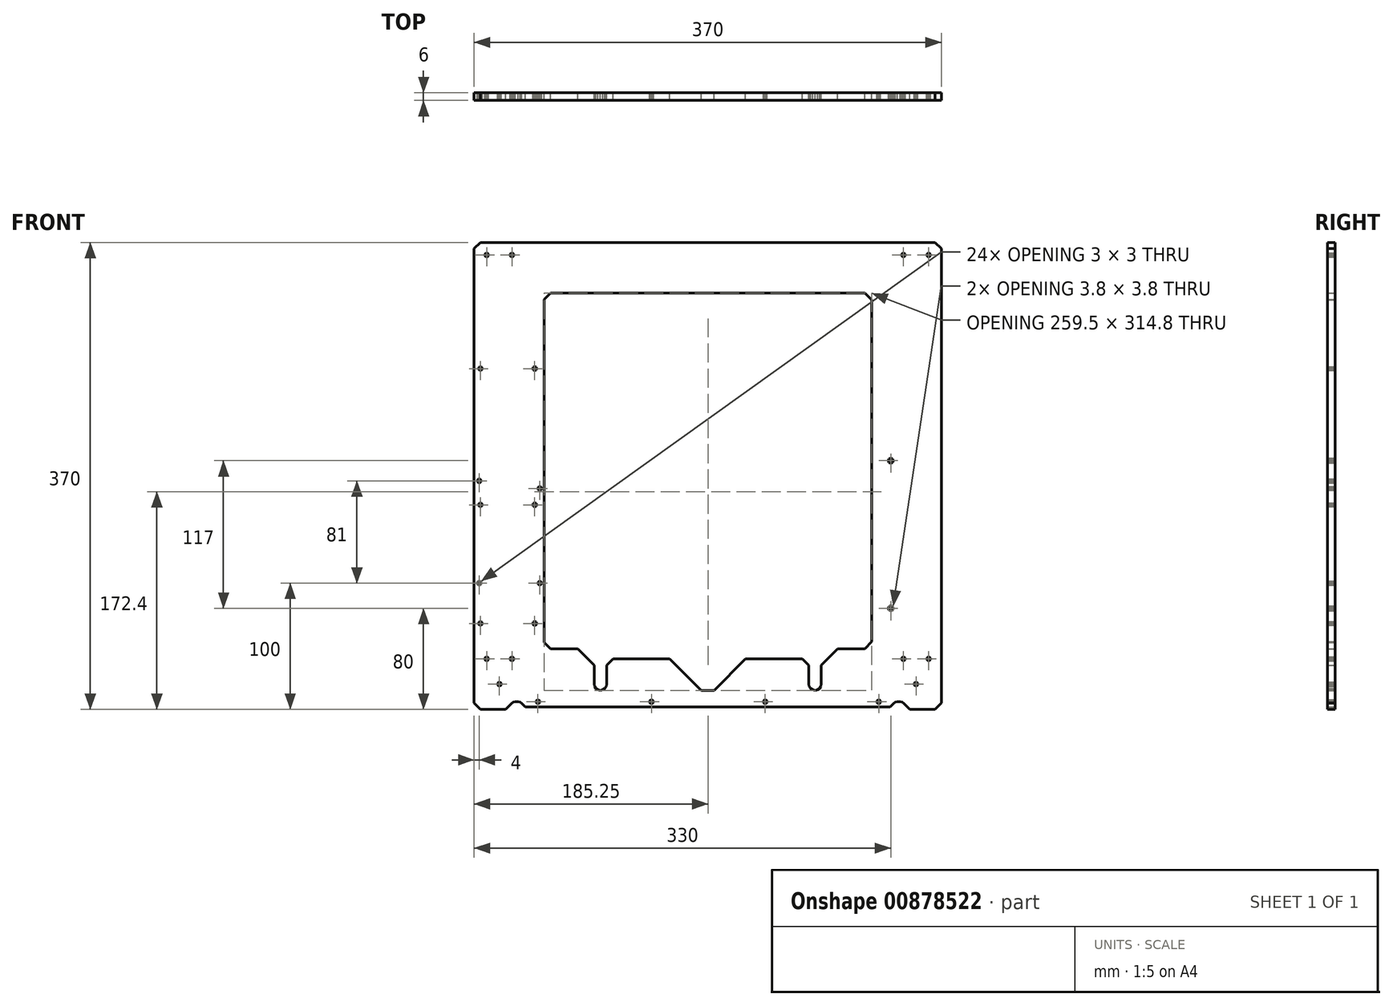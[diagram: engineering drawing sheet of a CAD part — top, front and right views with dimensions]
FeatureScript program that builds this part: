
annotation { "Feature Type Name" : "Feature", "Feature Type Description" : "" }
export const myFeature = defineFeature(function(context is Context, id is Id, definition is map)
    precondition{}
    {
        {
            var Q0;
            Q0=qCreatedBy(makeId("Front.planeOp"),FACE);
            var sketch = newSketch(context, id + "F0", { "sketchPlane" : qUnion([Q0])});
            skLineSegment(sketch, "E0", {"start": v(176.5, -145) * mm, "end": v(176.39, -145.57) * mm});
            skLineSegment(sketch, "E1", {"start": v(176.39, -145.57) * mm, "end": v(176.06, -146.06) * mm});
            skLineSegment(sketch, "E2", {"start": v(176.06, -146.06) * mm, "end": v(175.57, -146.39) * mm});
            skLineSegment(sketch, "E3", {"start": v(175.57, -146.39) * mm, "end": v(175, -146.5) * mm});
            skLineSegment(sketch, "E4", {"start": v(175, -146.5) * mm, "end": v(174.43, -146.39) * mm});
            skLineSegment(sketch, "E5", {"start": v(174.43, -146.39) * mm, "end": v(173.94, -146.06) * mm});
            skLineSegment(sketch, "E6", {"start": v(173.94, -146.06) * mm, "end": v(173.61, -145.57) * mm});
            skLineSegment(sketch, "E7", {"start": v(173.61, -145.57) * mm, "end": v(173.5, -145) * mm});
            skLineSegment(sketch, "E8", {"start": v(173.5, -145) * mm, "end": v(173.61, -144.43) * mm});
            skLineSegment(sketch, "E9", {"start": v(173.61, -144.43) * mm, "end": v(173.94, -143.94) * mm});
            skLineSegment(sketch, "E10", {"start": v(173.94, -143.94) * mm, "end": v(174.43, -143.61) * mm});
            skLineSegment(sketch, "E11", {"start": v(174.43, -143.61) * mm, "end": v(175, -143.5) * mm});
            skLineSegment(sketch, "E12", {"start": v(175, -143.5) * mm, "end": v(175.57, -143.61) * mm});
            skLineSegment(sketch, "E13", {"start": v(175.57, -143.61) * mm, "end": v(176.06, -143.94) * mm});
            skLineSegment(sketch, "E14", {"start": v(176.06, -143.94) * mm, "end": v(176.39, -144.43) * mm});
            skLineSegment(sketch, "E15", {"start": v(176.39, -144.43) * mm, "end": v(176.5, -145) * mm});
            skLineSegment(sketch, "E16", {"start": v(176.5, 175) * mm, "end": v(176.39, 174.43) * mm});
            skLineSegment(sketch, "E17", {"start": v(176.39, 174.43) * mm, "end": v(176.06, 173.94) * mm});
            skLineSegment(sketch, "E18", {"start": v(176.06, 173.94) * mm, "end": v(175.57, 173.61) * mm});
            skLineSegment(sketch, "E19", {"start": v(175.57, 173.61) * mm, "end": v(175, 173.5) * mm});
            skLineSegment(sketch, "E20", {"start": v(175, 173.5) * mm, "end": v(174.43, 173.61) * mm});
            skLineSegment(sketch, "E21", {"start": v(174.43, 173.61) * mm, "end": v(173.94, 173.94) * mm});
            skLineSegment(sketch, "E22", {"start": v(173.94, 173.94) * mm, "end": v(173.61, 174.43) * mm});
            skLineSegment(sketch, "E23", {"start": v(173.61, 174.43) * mm, "end": v(173.5, 175) * mm});
            skLineSegment(sketch, "E24", {"start": v(173.5, 175) * mm, "end": v(173.61, 175.57) * mm});
            skLineSegment(sketch, "E25", {"start": v(173.61, 175.57) * mm, "end": v(173.94, 176.06) * mm});
            skLineSegment(sketch, "E26", {"start": v(173.94, 176.06) * mm, "end": v(174.43, 176.39) * mm});
            skLineSegment(sketch, "E27", {"start": v(174.43, 176.39) * mm, "end": v(175, 176.5) * mm});
            skLineSegment(sketch, "E28", {"start": v(175, 176.5) * mm, "end": v(175.57, 176.39) * mm});
            skLineSegment(sketch, "E29", {"start": v(175.57, 176.39) * mm, "end": v(176.06, 176.06) * mm});
            skLineSegment(sketch, "E30", {"start": v(176.06, 176.06) * mm, "end": v(176.39, 175.57) * mm});
            skLineSegment(sketch, "E31", {"start": v(176.39, 175.57) * mm, "end": v(176.5, 175) * mm});
            skLineSegment(sketch, "E32", {"start": v(166.5, -165) * mm, "end": v(166.39, -165.57) * mm});
            skLineSegment(sketch, "E33", {"start": v(166.39, -165.57) * mm, "end": v(166.06, -166.06) * mm});
            skLineSegment(sketch, "E34", {"start": v(166.06, -166.06) * mm, "end": v(165.57, -166.39) * mm});
            skLineSegment(sketch, "E35", {"start": v(165.57, -166.39) * mm, "end": v(165, -166.5) * mm});
            skLineSegment(sketch, "E36", {"start": v(165, -166.5) * mm, "end": v(164.43, -166.39) * mm});
            skLineSegment(sketch, "E37", {"start": v(164.43, -166.39) * mm, "end": v(163.94, -166.06) * mm});
            skLineSegment(sketch, "E38", {"start": v(163.94, -166.06) * mm, "end": v(163.61, -165.57) * mm});
            skLineSegment(sketch, "E39", {"start": v(163.61, -165.57) * mm, "end": v(163.5, -165) * mm});
            skLineSegment(sketch, "E40", {"start": v(163.5, -165) * mm, "end": v(163.61, -164.43) * mm});
            skLineSegment(sketch, "E41", {"start": v(163.61, -164.43) * mm, "end": v(163.94, -163.94) * mm});
            skLineSegment(sketch, "E42", {"start": v(163.94, -163.94) * mm, "end": v(164.43, -163.61) * mm});
            skLineSegment(sketch, "E43", {"start": v(164.43, -163.61) * mm, "end": v(165, -163.5) * mm});
            skLineSegment(sketch, "E44", {"start": v(165, -163.5) * mm, "end": v(165.57, -163.61) * mm});
            skLineSegment(sketch, "E45", {"start": v(165.57, -163.61) * mm, "end": v(166.06, -163.94) * mm});
            skLineSegment(sketch, "E46", {"start": v(166.06, -163.94) * mm, "end": v(166.39, -164.43) * mm});
            skLineSegment(sketch, "E47", {"start": v(166.39, -164.43) * mm, "end": v(166.5, -165) * mm});
            skLineSegment(sketch, "E48", {"start": v(156.5, -145) * mm, "end": v(156.39, -145.57) * mm});
            skLineSegment(sketch, "E49", {"start": v(156.39, -145.57) * mm, "end": v(156.06, -146.06) * mm});
            skLineSegment(sketch, "E50", {"start": v(156.06, -146.06) * mm, "end": v(155.57, -146.39) * mm});
            skLineSegment(sketch, "E51", {"start": v(155.57, -146.39) * mm, "end": v(155, -146.5) * mm});
            skLineSegment(sketch, "E52", {"start": v(155, -146.5) * mm, "end": v(154.43, -146.39) * mm});
            skLineSegment(sketch, "E53", {"start": v(154.43, -146.39) * mm, "end": v(153.94, -146.06) * mm});
            skLineSegment(sketch, "E54", {"start": v(153.94, -146.06) * mm, "end": v(153.61, -145.57) * mm});
            skLineSegment(sketch, "E55", {"start": v(153.61, -145.57) * mm, "end": v(153.5, -145) * mm});
            skLineSegment(sketch, "E56", {"start": v(153.5, -145) * mm, "end": v(153.61, -144.43) * mm});
            skLineSegment(sketch, "E57", {"start": v(153.61, -144.43) * mm, "end": v(153.94, -143.94) * mm});
            skLineSegment(sketch, "E58", {"start": v(153.94, -143.94) * mm, "end": v(154.43, -143.61) * mm});
            skLineSegment(sketch, "E59", {"start": v(154.43, -143.61) * mm, "end": v(155, -143.5) * mm});
            skLineSegment(sketch, "E60", {"start": v(155, -143.5) * mm, "end": v(155.57, -143.61) * mm});
            skLineSegment(sketch, "E61", {"start": v(155.57, -143.61) * mm, "end": v(156.06, -143.94) * mm});
            skLineSegment(sketch, "E62", {"start": v(156.06, -143.94) * mm, "end": v(156.39, -144.43) * mm});
            skLineSegment(sketch, "E63", {"start": v(156.39, -144.43) * mm, "end": v(156.5, -145) * mm});
            skLineSegment(sketch, "E64", {"start": v(146.9, -105) * mm, "end": v(146.76, -105.73) * mm});
            skLineSegment(sketch, "E65", {"start": v(146.76, -105.73) * mm, "end": v(146.34, -106.34) * mm});
            skLineSegment(sketch, "E66", {"start": v(146.34, -106.34) * mm, "end": v(145.73, -106.76) * mm});
            skLineSegment(sketch, "E67", {"start": v(145.73, -106.76) * mm, "end": v(145, -106.9) * mm});
            skLineSegment(sketch, "E68", {"start": v(145, -106.9) * mm, "end": v(144.27, -106.76) * mm});
            skLineSegment(sketch, "E69", {"start": v(144.27, -106.76) * mm, "end": v(143.66, -106.34) * mm});
            skLineSegment(sketch, "E70", {"start": v(143.66, -106.34) * mm, "end": v(143.24, -105.73) * mm});
            skLineSegment(sketch, "E71", {"start": v(143.24, -105.73) * mm, "end": v(143.1, -105) * mm});
            skLineSegment(sketch, "E72", {"start": v(143.1, -105) * mm, "end": v(143.24, -104.27) * mm});
            skLineSegment(sketch, "E73", {"start": v(143.24, -104.27) * mm, "end": v(143.66, -103.66) * mm});
            skLineSegment(sketch, "E74", {"start": v(143.66, -103.66) * mm, "end": v(144.27, -103.24) * mm});
            skLineSegment(sketch, "E75", {"start": v(144.27, -103.24) * mm, "end": v(145, -103.1) * mm});
            skLineSegment(sketch, "E76", {"start": v(145, -103.1) * mm, "end": v(145.73, -103.24) * mm});
            skLineSegment(sketch, "E77", {"start": v(145.73, -103.24) * mm, "end": v(146.34, -103.66) * mm});
            skLineSegment(sketch, "E78", {"start": v(146.34, -103.66) * mm, "end": v(146.76, -104.27) * mm});
            skLineSegment(sketch, "E79", {"start": v(146.76, -104.27) * mm, "end": v(146.9, -105) * mm});
            skLineSegment(sketch, "E80", {"start": v(137, -179) * mm, "end": v(136.89, -179.57) * mm});
            skLineSegment(sketch, "E81", {"start": v(136.89, -179.57) * mm, "end": v(136.56, -180.06) * mm});
            skLineSegment(sketch, "E82", {"start": v(136.56, -180.06) * mm, "end": v(136.07, -180.39) * mm});
            skLineSegment(sketch, "E83", {"start": v(136.07, -180.39) * mm, "end": v(135.5, -180.5) * mm});
            skLineSegment(sketch, "E84", {"start": v(135.5, -180.5) * mm, "end": v(134.93, -180.39) * mm});
            skLineSegment(sketch, "E85", {"start": v(134.93, -180.39) * mm, "end": v(134.44, -180.06) * mm});
            skLineSegment(sketch, "E86", {"start": v(134.44, -180.06) * mm, "end": v(134.11, -179.57) * mm});
            skLineSegment(sketch, "E87", {"start": v(134.11, -179.57) * mm, "end": v(134, -179) * mm});
            skLineSegment(sketch, "E88", {"start": v(134, -179) * mm, "end": v(134.11, -178.43) * mm});
            skLineSegment(sketch, "E89", {"start": v(134.11, -178.43) * mm, "end": v(134.44, -177.94) * mm});
            skLineSegment(sketch, "E90", {"start": v(134.44, -177.94) * mm, "end": v(134.93, -177.61) * mm});
            skLineSegment(sketch, "E91", {"start": v(134.93, -177.61) * mm, "end": v(135.5, -177.5) * mm});
            skLineSegment(sketch, "E92", {"start": v(135.5, -177.5) * mm, "end": v(136.07, -177.61) * mm});
            skLineSegment(sketch, "E93", {"start": v(136.07, -177.61) * mm, "end": v(136.56, -177.94) * mm});
            skLineSegment(sketch, "E94", {"start": v(136.56, -177.94) * mm, "end": v(136.89, -178.43) * mm});
            skLineSegment(sketch, "E95", {"start": v(136.89, -178.43) * mm, "end": v(137, -179) * mm});
            skLineSegment(sketch, "E96", {"start": v(146.9, 12) * mm, "end": v(146.76, 11.27) * mm});
            skLineSegment(sketch, "E97", {"start": v(146.76, 11.27) * mm, "end": v(146.34, 10.66) * mm});
            skLineSegment(sketch, "E98", {"start": v(146.34, 10.66) * mm, "end": v(145.73, 10.24) * mm});
            skLineSegment(sketch, "E99", {"start": v(145.73, 10.24) * mm, "end": v(145, 10.1) * mm});
            skLineSegment(sketch, "E100", {"start": v(145, 10.1) * mm, "end": v(144.27, 10.24) * mm});
            skLineSegment(sketch, "E101", {"start": v(144.27, 10.24) * mm, "end": v(143.66, 10.66) * mm});
            skLineSegment(sketch, "E102", {"start": v(143.66, 10.66) * mm, "end": v(143.24, 11.27) * mm});
            skLineSegment(sketch, "E103", {"start": v(143.24, 11.27) * mm, "end": v(143.1, 12) * mm});
            skLineSegment(sketch, "E104", {"start": v(143.1, 12) * mm, "end": v(143.24, 12.73) * mm});
            skLineSegment(sketch, "E105", {"start": v(143.24, 12.73) * mm, "end": v(143.66, 13.34) * mm});
            skLineSegment(sketch, "E106", {"start": v(143.66, 13.34) * mm, "end": v(144.27, 13.76) * mm});
            skLineSegment(sketch, "E107", {"start": v(144.27, 13.76) * mm, "end": v(145, 13.9) * mm});
            skLineSegment(sketch, "E108", {"start": v(145, 13.9) * mm, "end": v(145.73, 13.76) * mm});
            skLineSegment(sketch, "E109", {"start": v(145.73, 13.76) * mm, "end": v(146.34, 13.34) * mm});
            skLineSegment(sketch, "E110", {"start": v(146.34, 13.34) * mm, "end": v(146.76, 12.73) * mm});
            skLineSegment(sketch, "E111", {"start": v(146.76, 12.73) * mm, "end": v(146.9, 12) * mm});
            skLineSegment(sketch, "E112", {"start": v(156.5, 175) * mm, "end": v(156.39, 174.43) * mm});
            skLineSegment(sketch, "E113", {"start": v(156.39, 174.43) * mm, "end": v(156.06, 173.94) * mm});
            skLineSegment(sketch, "E114", {"start": v(156.06, 173.94) * mm, "end": v(155.57, 173.61) * mm});
            skLineSegment(sketch, "E115", {"start": v(155.57, 173.61) * mm, "end": v(155, 173.5) * mm});
            skLineSegment(sketch, "E116", {"start": v(155, 173.5) * mm, "end": v(154.43, 173.61) * mm});
            skLineSegment(sketch, "E117", {"start": v(154.43, 173.61) * mm, "end": v(153.94, 173.94) * mm});
            skLineSegment(sketch, "E118", {"start": v(153.94, 173.94) * mm, "end": v(153.61, 174.43) * mm});
            skLineSegment(sketch, "E119", {"start": v(153.61, 174.43) * mm, "end": v(153.5, 175) * mm});
            skLineSegment(sketch, "E120", {"start": v(153.5, 175) * mm, "end": v(153.61, 175.57) * mm});
            skLineSegment(sketch, "E121", {"start": v(153.61, 175.57) * mm, "end": v(153.94, 176.06) * mm});
            skLineSegment(sketch, "E122", {"start": v(153.94, 176.06) * mm, "end": v(154.43, 176.39) * mm});
            skLineSegment(sketch, "E123", {"start": v(154.43, 176.39) * mm, "end": v(155, 176.5) * mm});
            skLineSegment(sketch, "E124", {"start": v(155, 176.5) * mm, "end": v(155.57, 176.39) * mm});
            skLineSegment(sketch, "E125", {"start": v(155.57, 176.39) * mm, "end": v(156.06, 176.06) * mm});
            skLineSegment(sketch, "E126", {"start": v(156.06, 176.06) * mm, "end": v(156.39, 175.57) * mm});
            skLineSegment(sketch, "E127", {"start": v(156.39, 175.57) * mm, "end": v(156.5, 175) * mm});
            skLineSegment(sketch, "E128", {"start": v(-153.5, 175) * mm, "end": v(-153.61, 174.43) * mm});
            skLineSegment(sketch, "E129", {"start": v(-153.61, 174.43) * mm, "end": v(-153.94, 173.94) * mm});
            skLineSegment(sketch, "E130", {"start": v(-153.94, 173.94) * mm, "end": v(-154.43, 173.61) * mm});
            skLineSegment(sketch, "E131", {"start": v(-154.43, 173.61) * mm, "end": v(-155, 173.5) * mm});
            skLineSegment(sketch, "E132", {"start": v(-155, 173.5) * mm, "end": v(-155.57, 173.61) * mm});
            skLineSegment(sketch, "E133", {"start": v(-155.57, 173.61) * mm, "end": v(-156.06, 173.94) * mm});
            skLineSegment(sketch, "E134", {"start": v(-156.06, 173.94) * mm, "end": v(-156.39, 174.43) * mm});
            skLineSegment(sketch, "E135", {"start": v(-156.39, 174.43) * mm, "end": v(-156.5, 175) * mm});
            skLineSegment(sketch, "E136", {"start": v(-156.5, 175) * mm, "end": v(-156.39, 175.57) * mm});
            skLineSegment(sketch, "E137", {"start": v(-156.39, 175.57) * mm, "end": v(-156.06, 176.06) * mm});
            skLineSegment(sketch, "E138", {"start": v(-156.06, 176.06) * mm, "end": v(-155.57, 176.39) * mm});
            skLineSegment(sketch, "E139", {"start": v(-155.57, 176.39) * mm, "end": v(-155, 176.5) * mm});
            skLineSegment(sketch, "E140", {"start": v(-155, 176.5) * mm, "end": v(-154.43, 176.39) * mm});
            skLineSegment(sketch, "E141", {"start": v(-154.43, 176.39) * mm, "end": v(-153.94, 176.06) * mm});
            skLineSegment(sketch, "E142", {"start": v(-153.94, 176.06) * mm, "end": v(-153.61, 175.57) * mm});
            skLineSegment(sketch, "E143", {"start": v(-153.61, 175.57) * mm, "end": v(-153.5, 175) * mm});
            skLineSegment(sketch, "E144", {"start": v(-173.5, 175) * mm, "end": v(-173.61, 174.43) * mm});
            skLineSegment(sketch, "E145", {"start": v(-173.61, 174.43) * mm, "end": v(-173.94, 173.94) * mm});
            skLineSegment(sketch, "E146", {"start": v(-173.94, 173.94) * mm, "end": v(-174.43, 173.61) * mm});
            skLineSegment(sketch, "E147", {"start": v(-174.43, 173.61) * mm, "end": v(-175, 173.5) * mm});
            skLineSegment(sketch, "E148", {"start": v(-175, 173.5) * mm, "end": v(-175.57, 173.61) * mm});
            skLineSegment(sketch, "E149", {"start": v(-175.57, 173.61) * mm, "end": v(-176.06, 173.94) * mm});
            skLineSegment(sketch, "E150", {"start": v(-176.06, 173.94) * mm, "end": v(-176.39, 174.43) * mm});
            skLineSegment(sketch, "E151", {"start": v(-176.39, 174.43) * mm, "end": v(-176.5, 175) * mm});
            skLineSegment(sketch, "E152", {"start": v(-176.5, 175) * mm, "end": v(-176.39, 175.57) * mm});
            skLineSegment(sketch, "E153", {"start": v(-176.39, 175.57) * mm, "end": v(-176.06, 176.06) * mm});
            skLineSegment(sketch, "E154", {"start": v(-176.06, 176.06) * mm, "end": v(-175.57, 176.39) * mm});
            skLineSegment(sketch, "E155", {"start": v(-175.57, 176.39) * mm, "end": v(-175, 176.5) * mm});
            skLineSegment(sketch, "E156", {"start": v(-175, 176.5) * mm, "end": v(-174.43, 176.39) * mm});
            skLineSegment(sketch, "E157", {"start": v(-174.43, 176.39) * mm, "end": v(-173.94, 176.06) * mm});
            skLineSegment(sketch, "E158", {"start": v(-173.94, 176.06) * mm, "end": v(-173.61, 175.57) * mm});
            skLineSegment(sketch, "E159", {"start": v(-173.61, 175.57) * mm, "end": v(-173.5, 175) * mm});
            skLineSegment(sketch, "E160", {"start": v(-131.5, -10) * mm, "end": v(-131.61, -10.57) * mm});
            skLineSegment(sketch, "E161", {"start": v(-131.61, -10.57) * mm, "end": v(-131.94, -11.06) * mm});
            skLineSegment(sketch, "E162", {"start": v(-131.94, -11.06) * mm, "end": v(-132.43, -11.39) * mm});
            skLineSegment(sketch, "E163", {"start": v(-132.43, -11.39) * mm, "end": v(-133, -11.5) * mm});
            skLineSegment(sketch, "E164", {"start": v(-133, -11.5) * mm, "end": v(-133.57, -11.39) * mm});
            skLineSegment(sketch, "E165", {"start": v(-133.57, -11.39) * mm, "end": v(-134.06, -11.06) * mm});
            skLineSegment(sketch, "E166", {"start": v(-134.06, -11.06) * mm, "end": v(-134.39, -10.57) * mm});
            skLineSegment(sketch, "E167", {"start": v(-134.39, -10.57) * mm, "end": v(-134.5, -10) * mm});
            skLineSegment(sketch, "E168", {"start": v(-134.5, -10) * mm, "end": v(-134.39, -9.43) * mm});
            skLineSegment(sketch, "E169", {"start": v(-134.39, -9.43) * mm, "end": v(-134.06, -8.94) * mm});
            skLineSegment(sketch, "E170", {"start": v(-134.06, -8.94) * mm, "end": v(-133.57, -8.61) * mm});
            skLineSegment(sketch, "E171", {"start": v(-133.57, -8.61) * mm, "end": v(-133, -8.5) * mm});
            skLineSegment(sketch, "E172", {"start": v(-133, -8.5) * mm, "end": v(-132.43, -8.61) * mm});
            skLineSegment(sketch, "E173", {"start": v(-132.43, -8.61) * mm, "end": v(-131.94, -8.94) * mm});
            skLineSegment(sketch, "E174", {"start": v(-131.94, -8.94) * mm, "end": v(-131.61, -9.43) * mm});
            skLineSegment(sketch, "E175", {"start": v(-131.61, -9.43) * mm, "end": v(-131.5, -10) * mm});
            skLineSegment(sketch, "E176", {"start": v(-179.5, -4) * mm, "end": v(-179.61, -4.57) * mm});
            skLineSegment(sketch, "E177", {"start": v(-179.61, -4.57) * mm, "end": v(-179.94, -5.06) * mm});
            skLineSegment(sketch, "E178", {"start": v(-179.94, -5.06) * mm, "end": v(-180.43, -5.39) * mm});
            skLineSegment(sketch, "E179", {"start": v(-180.43, -5.39) * mm, "end": v(-181, -5.5) * mm});
            skLineSegment(sketch, "E180", {"start": v(-181, -5.5) * mm, "end": v(-181.57, -5.39) * mm});
            skLineSegment(sketch, "E181", {"start": v(-181.57, -5.39) * mm, "end": v(-182.06, -5.06) * mm});
            skLineSegment(sketch, "E182", {"start": v(-182.06, -5.06) * mm, "end": v(-182.39, -4.57) * mm});
            skLineSegment(sketch, "E183", {"start": v(-182.39, -4.57) * mm, "end": v(-182.5, -4) * mm});
            skLineSegment(sketch, "E184", {"start": v(-182.5, -4) * mm, "end": v(-182.39, -3.43) * mm});
            skLineSegment(sketch, "E185", {"start": v(-182.39, -3.43) * mm, "end": v(-182.06, -2.94) * mm});
            skLineSegment(sketch, "E186", {"start": v(-182.06, -2.94) * mm, "end": v(-181.57, -2.61) * mm});
            skLineSegment(sketch, "E187", {"start": v(-181.57, -2.61) * mm, "end": v(-181, -2.5) * mm});
            skLineSegment(sketch, "E188", {"start": v(-181, -2.5) * mm, "end": v(-180.43, -2.61) * mm});
            skLineSegment(sketch, "E189", {"start": v(-180.43, -2.61) * mm, "end": v(-179.94, -2.94) * mm});
            skLineSegment(sketch, "E190", {"start": v(-179.94, -2.94) * mm, "end": v(-179.61, -3.43) * mm});
            skLineSegment(sketch, "E191", {"start": v(-179.61, -3.43) * mm, "end": v(-179.5, -4) * mm});
            skLineSegment(sketch, "E192", {"start": v(-135.5, 85) * mm, "end": v(-135.61, 84.43) * mm});
            skLineSegment(sketch, "E193", {"start": v(-135.61, 84.43) * mm, "end": v(-135.94, 83.94) * mm});
            skLineSegment(sketch, "E194", {"start": v(-135.94, 83.94) * mm, "end": v(-136.43, 83.61) * mm});
            skLineSegment(sketch, "E195", {"start": v(-136.43, 83.61) * mm, "end": v(-137, 83.5) * mm});
            skLineSegment(sketch, "E196", {"start": v(-137, 83.5) * mm, "end": v(-137.57, 83.61) * mm});
            skLineSegment(sketch, "E197", {"start": v(-137.57, 83.61) * mm, "end": v(-138.06, 83.94) * mm});
            skLineSegment(sketch, "E198", {"start": v(-138.06, 83.94) * mm, "end": v(-138.39, 84.43) * mm});
            skLineSegment(sketch, "E199", {"start": v(-138.39, 84.43) * mm, "end": v(-138.5, 85) * mm});
            skLineSegment(sketch, "E200", {"start": v(-138.5, 85) * mm, "end": v(-138.39, 85.57) * mm});
            skLineSegment(sketch, "E201", {"start": v(-138.39, 85.57) * mm, "end": v(-138.06, 86.06) * mm});
            skLineSegment(sketch, "E202", {"start": v(-138.06, 86.06) * mm, "end": v(-137.57, 86.39) * mm});
            skLineSegment(sketch, "E203", {"start": v(-137.57, 86.39) * mm, "end": v(-137, 86.5) * mm});
            skLineSegment(sketch, "E204", {"start": v(-137, 86.5) * mm, "end": v(-136.43, 86.39) * mm});
            skLineSegment(sketch, "E205", {"start": v(-136.43, 86.39) * mm, "end": v(-135.94, 86.06) * mm});
            skLineSegment(sketch, "E206", {"start": v(-135.94, 86.06) * mm, "end": v(-135.61, 85.57) * mm});
            skLineSegment(sketch, "E207", {"start": v(-135.61, 85.57) * mm, "end": v(-135.5, 85) * mm});
            skLineSegment(sketch, "E208", {"start": v(-178.5, 85) * mm, "end": v(-178.61, 84.43) * mm});
            skLineSegment(sketch, "E209", {"start": v(-178.61, 84.43) * mm, "end": v(-178.94, 83.94) * mm});
            skLineSegment(sketch, "E210", {"start": v(-178.94, 83.94) * mm, "end": v(-179.43, 83.61) * mm});
            skLineSegment(sketch, "E211", {"start": v(-179.43, 83.61) * mm, "end": v(-180, 83.5) * mm});
            skLineSegment(sketch, "E212", {"start": v(-180, 83.5) * mm, "end": v(-180.57, 83.61) * mm});
            skLineSegment(sketch, "E213", {"start": v(-180.57, 83.61) * mm, "end": v(-181.06, 83.94) * mm});
            skLineSegment(sketch, "E214", {"start": v(-181.06, 83.94) * mm, "end": v(-181.39, 84.43) * mm});
            skLineSegment(sketch, "E215", {"start": v(-181.39, 84.43) * mm, "end": v(-181.5, 85) * mm});
            skLineSegment(sketch, "E216", {"start": v(-181.5, 85) * mm, "end": v(-181.39, 85.57) * mm});
            skLineSegment(sketch, "E217", {"start": v(-181.39, 85.57) * mm, "end": v(-181.06, 86.06) * mm});
            skLineSegment(sketch, "E218", {"start": v(-181.06, 86.06) * mm, "end": v(-180.57, 86.39) * mm});
            skLineSegment(sketch, "E219", {"start": v(-180.57, 86.39) * mm, "end": v(-180, 86.5) * mm});
            skLineSegment(sketch, "E220", {"start": v(-180, 86.5) * mm, "end": v(-179.43, 86.39) * mm});
            skLineSegment(sketch, "E221", {"start": v(-179.43, 86.39) * mm, "end": v(-178.94, 86.06) * mm});
            skLineSegment(sketch, "E222", {"start": v(-178.94, 86.06) * mm, "end": v(-178.61, 85.57) * mm});
            skLineSegment(sketch, "E223", {"start": v(-178.61, 85.57) * mm, "end": v(-178.5, 85) * mm});
            skLineSegment(sketch, "E224", {"start": v(-153.5, -145) * mm, "end": v(-153.61, -145.57) * mm});
            skLineSegment(sketch, "E225", {"start": v(-153.61, -145.57) * mm, "end": v(-153.94, -146.06) * mm});
            skLineSegment(sketch, "E226", {"start": v(-153.94, -146.06) * mm, "end": v(-154.43, -146.39) * mm});
            skLineSegment(sketch, "E227", {"start": v(-154.43, -146.39) * mm, "end": v(-155, -146.5) * mm});
            skLineSegment(sketch, "E228", {"start": v(-155, -146.5) * mm, "end": v(-155.57, -146.39) * mm});
            skLineSegment(sketch, "E229", {"start": v(-155.57, -146.39) * mm, "end": v(-156.06, -146.06) * mm});
            skLineSegment(sketch, "E230", {"start": v(-156.06, -146.06) * mm, "end": v(-156.39, -145.57) * mm});
            skLineSegment(sketch, "E231", {"start": v(-156.39, -145.57) * mm, "end": v(-156.5, -145) * mm});
            skLineSegment(sketch, "E232", {"start": v(-156.5, -145) * mm, "end": v(-156.39, -144.43) * mm});
            skLineSegment(sketch, "E233", {"start": v(-156.39, -144.43) * mm, "end": v(-156.06, -143.94) * mm});
            skLineSegment(sketch, "E234", {"start": v(-156.06, -143.94) * mm, "end": v(-155.57, -143.61) * mm});
            skLineSegment(sketch, "E235", {"start": v(-155.57, -143.61) * mm, "end": v(-155, -143.5) * mm});
            skLineSegment(sketch, "E236", {"start": v(-155, -143.5) * mm, "end": v(-154.43, -143.61) * mm});
            skLineSegment(sketch, "E237", {"start": v(-154.43, -143.61) * mm, "end": v(-153.94, -143.94) * mm});
            skLineSegment(sketch, "E238", {"start": v(-153.94, -143.94) * mm, "end": v(-153.61, -144.43) * mm});
            skLineSegment(sketch, "E239", {"start": v(-153.61, -144.43) * mm, "end": v(-153.5, -145) * mm});
            skLineSegment(sketch, "E240", {"start": v(-135.5, -23) * mm, "end": v(-135.61, -23.57) * mm});
            skLineSegment(sketch, "E241", {"start": v(-135.61, -23.57) * mm, "end": v(-135.94, -24.06) * mm});
            skLineSegment(sketch, "E242", {"start": v(-135.94, -24.06) * mm, "end": v(-136.43, -24.39) * mm});
            skLineSegment(sketch, "E243", {"start": v(-136.43, -24.39) * mm, "end": v(-137, -24.5) * mm});
            skLineSegment(sketch, "E244", {"start": v(-137, -24.5) * mm, "end": v(-137.57, -24.39) * mm});
            skLineSegment(sketch, "E245", {"start": v(-137.57, -24.39) * mm, "end": v(-138.06, -24.06) * mm});
            skLineSegment(sketch, "E246", {"start": v(-138.06, -24.06) * mm, "end": v(-138.39, -23.57) * mm});
            skLineSegment(sketch, "E247", {"start": v(-138.39, -23.57) * mm, "end": v(-138.5, -23) * mm});
            skLineSegment(sketch, "E248", {"start": v(-138.5, -23) * mm, "end": v(-138.39, -22.43) * mm});
            skLineSegment(sketch, "E249", {"start": v(-138.39, -22.43) * mm, "end": v(-138.06, -21.94) * mm});
            skLineSegment(sketch, "E250", {"start": v(-138.06, -21.94) * mm, "end": v(-137.57, -21.61) * mm});
            skLineSegment(sketch, "E251", {"start": v(-137.57, -21.61) * mm, "end": v(-137, -21.5) * mm});
            skLineSegment(sketch, "E252", {"start": v(-137, -21.5) * mm, "end": v(-136.43, -21.61) * mm});
            skLineSegment(sketch, "E253", {"start": v(-136.43, -21.61) * mm, "end": v(-135.94, -21.94) * mm});
            skLineSegment(sketch, "E254", {"start": v(-135.94, -21.94) * mm, "end": v(-135.61, -22.43) * mm});
            skLineSegment(sketch, "E255", {"start": v(-135.61, -22.43) * mm, "end": v(-135.5, -23) * mm});
            skLineSegment(sketch, "E256", {"start": v(-131.5, -85) * mm, "end": v(-131.61, -85.57) * mm});
            skLineSegment(sketch, "E257", {"start": v(-131.61, -85.57) * mm, "end": v(-131.94, -86.06) * mm});
            skLineSegment(sketch, "E258", {"start": v(-131.94, -86.06) * mm, "end": v(-132.43, -86.39) * mm});
            skLineSegment(sketch, "E259", {"start": v(-132.43, -86.39) * mm, "end": v(-133, -86.5) * mm});
            skLineSegment(sketch, "E260", {"start": v(-133, -86.5) * mm, "end": v(-133.57, -86.39) * mm});
            skLineSegment(sketch, "E261", {"start": v(-133.57, -86.39) * mm, "end": v(-134.06, -86.06) * mm});
            skLineSegment(sketch, "E262", {"start": v(-134.06, -86.06) * mm, "end": v(-134.39, -85.57) * mm});
            skLineSegment(sketch, "E263", {"start": v(-134.39, -85.57) * mm, "end": v(-134.5, -85) * mm});
            skLineSegment(sketch, "E264", {"start": v(-134.5, -85) * mm, "end": v(-134.39, -84.43) * mm});
            skLineSegment(sketch, "E265", {"start": v(-134.39, -84.43) * mm, "end": v(-134.06, -83.94) * mm});
            skLineSegment(sketch, "E266", {"start": v(-134.06, -83.94) * mm, "end": v(-133.57, -83.61) * mm});
            skLineSegment(sketch, "E267", {"start": v(-133.57, -83.61) * mm, "end": v(-133, -83.5) * mm});
            skLineSegment(sketch, "E268", {"start": v(-133, -83.5) * mm, "end": v(-132.43, -83.61) * mm});
            skLineSegment(sketch, "E269", {"start": v(-132.43, -83.61) * mm, "end": v(-131.94, -83.94) * mm});
            skLineSegment(sketch, "E270", {"start": v(-131.94, -83.94) * mm, "end": v(-131.61, -84.43) * mm});
            skLineSegment(sketch, "E271", {"start": v(-131.61, -84.43) * mm, "end": v(-131.5, -85) * mm});
            skLineSegment(sketch, "E272", {"start": v(-178.5, -117) * mm, "end": v(-178.61, -117.57) * mm});
            skLineSegment(sketch, "E273", {"start": v(-178.61, -117.57) * mm, "end": v(-178.94, -118.06) * mm});
            skLineSegment(sketch, "E274", {"start": v(-178.94, -118.06) * mm, "end": v(-179.43, -118.39) * mm});
            skLineSegment(sketch, "E275", {"start": v(-179.43, -118.39) * mm, "end": v(-180, -118.5) * mm});
            skLineSegment(sketch, "E276", {"start": v(-180, -118.5) * mm, "end": v(-180.57, -118.39) * mm});
            skLineSegment(sketch, "E277", {"start": v(-180.57, -118.39) * mm, "end": v(-181.06, -118.06) * mm});
            skLineSegment(sketch, "E278", {"start": v(-181.06, -118.06) * mm, "end": v(-181.39, -117.57) * mm});
            skLineSegment(sketch, "E279", {"start": v(-181.39, -117.57) * mm, "end": v(-181.5, -117) * mm});
            skLineSegment(sketch, "E280", {"start": v(-181.5, -117) * mm, "end": v(-181.39, -116.43) * mm});
            skLineSegment(sketch, "E281", {"start": v(-181.39, -116.43) * mm, "end": v(-181.06, -115.94) * mm});
            skLineSegment(sketch, "E282", {"start": v(-181.06, -115.94) * mm, "end": v(-180.57, -115.61) * mm});
            skLineSegment(sketch, "E283", {"start": v(-180.57, -115.61) * mm, "end": v(-180, -115.5) * mm});
            skLineSegment(sketch, "E284", {"start": v(-180, -115.5) * mm, "end": v(-179.43, -115.61) * mm});
            skLineSegment(sketch, "E285", {"start": v(-179.43, -115.61) * mm, "end": v(-178.94, -115.94) * mm});
            skLineSegment(sketch, "E286", {"start": v(-178.94, -115.94) * mm, "end": v(-178.61, -116.43) * mm});
            skLineSegment(sketch, "E287", {"start": v(-178.61, -116.43) * mm, "end": v(-178.5, -117) * mm});
            skLineSegment(sketch, "E288", {"start": v(-173.5, -145) * mm, "end": v(-173.61, -145.57) * mm});
            skLineSegment(sketch, "E289", {"start": v(-173.61, -145.57) * mm, "end": v(-173.94, -146.06) * mm});
            skLineSegment(sketch, "E290", {"start": v(-173.94, -146.06) * mm, "end": v(-174.43, -146.39) * mm});
            skLineSegment(sketch, "E291", {"start": v(-174.43, -146.39) * mm, "end": v(-175, -146.5) * mm});
            skLineSegment(sketch, "E292", {"start": v(-175, -146.5) * mm, "end": v(-175.57, -146.39) * mm});
            skLineSegment(sketch, "E293", {"start": v(-175.57, -146.39) * mm, "end": v(-176.06, -146.06) * mm});
            skLineSegment(sketch, "E294", {"start": v(-176.06, -146.06) * mm, "end": v(-176.39, -145.57) * mm});
            skLineSegment(sketch, "E295", {"start": v(-176.39, -145.57) * mm, "end": v(-176.5, -145) * mm});
            skLineSegment(sketch, "E296", {"start": v(-176.5, -145) * mm, "end": v(-176.39, -144.43) * mm});
            skLineSegment(sketch, "E297", {"start": v(-176.39, -144.43) * mm, "end": v(-176.06, -143.94) * mm});
            skLineSegment(sketch, "E298", {"start": v(-176.06, -143.94) * mm, "end": v(-175.57, -143.61) * mm});
            skLineSegment(sketch, "E299", {"start": v(-175.57, -143.61) * mm, "end": v(-175, -143.5) * mm});
            skLineSegment(sketch, "E300", {"start": v(-175, -143.5) * mm, "end": v(-174.43, -143.61) * mm});
            skLineSegment(sketch, "E301", {"start": v(-174.43, -143.61) * mm, "end": v(-173.94, -143.94) * mm});
            skLineSegment(sketch, "E302", {"start": v(-173.94, -143.94) * mm, "end": v(-173.61, -144.43) * mm});
            skLineSegment(sketch, "E303", {"start": v(-173.61, -144.43) * mm, "end": v(-173.5, -145) * mm});
            skLineSegment(sketch, "E304", {"start": v(-179.5, -85) * mm, "end": v(-179.61, -85.57) * mm});
            skLineSegment(sketch, "E305", {"start": v(-179.61, -85.57) * mm, "end": v(-179.94, -86.06) * mm});
            skLineSegment(sketch, "E306", {"start": v(-179.94, -86.06) * mm, "end": v(-180.43, -86.39) * mm});
            skLineSegment(sketch, "E307", {"start": v(-180.43, -86.39) * mm, "end": v(-181, -86.5) * mm});
            skLineSegment(sketch, "E308", {"start": v(-181, -86.5) * mm, "end": v(-181.57, -86.39) * mm});
            skLineSegment(sketch, "E309", {"start": v(-181.57, -86.39) * mm, "end": v(-182.06, -86.06) * mm});
            skLineSegment(sketch, "E310", {"start": v(-182.06, -86.06) * mm, "end": v(-182.39, -85.57) * mm});
            skLineSegment(sketch, "E311", {"start": v(-182.39, -85.57) * mm, "end": v(-182.5, -85) * mm});
            skLineSegment(sketch, "E312", {"start": v(-182.5, -85) * mm, "end": v(-182.39, -84.43) * mm});
            skLineSegment(sketch, "E313", {"start": v(-182.39, -84.43) * mm, "end": v(-182.06, -83.94) * mm});
            skLineSegment(sketch, "E314", {"start": v(-182.06, -83.94) * mm, "end": v(-181.57, -83.61) * mm});
            skLineSegment(sketch, "E315", {"start": v(-181.57, -83.61) * mm, "end": v(-181, -83.5) * mm});
            skLineSegment(sketch, "E316", {"start": v(-181, -83.5) * mm, "end": v(-180.43, -83.61) * mm});
            skLineSegment(sketch, "E317", {"start": v(-180.43, -83.61) * mm, "end": v(-179.94, -83.94) * mm});
            skLineSegment(sketch, "E318", {"start": v(-179.94, -83.94) * mm, "end": v(-179.61, -84.43) * mm});
            skLineSegment(sketch, "E319", {"start": v(-179.61, -84.43) * mm, "end": v(-179.5, -85) * mm});
            skLineSegment(sketch, "E320", {"start": v(-178.5, -23) * mm, "end": v(-178.61, -23.57) * mm});
            skLineSegment(sketch, "E321", {"start": v(-178.61, -23.57) * mm, "end": v(-178.94, -24.06) * mm});
            skLineSegment(sketch, "E322", {"start": v(-178.94, -24.06) * mm, "end": v(-179.43, -24.39) * mm});
            skLineSegment(sketch, "E323", {"start": v(-179.43, -24.39) * mm, "end": v(-180, -24.5) * mm});
            skLineSegment(sketch, "E324", {"start": v(-180, -24.5) * mm, "end": v(-180.57, -24.39) * mm});
            skLineSegment(sketch, "E325", {"start": v(-180.57, -24.39) * mm, "end": v(-181.06, -24.06) * mm});
            skLineSegment(sketch, "E326", {"start": v(-181.06, -24.06) * mm, "end": v(-181.39, -23.57) * mm});
            skLineSegment(sketch, "E327", {"start": v(-181.39, -23.57) * mm, "end": v(-181.5, -23) * mm});
            skLineSegment(sketch, "E328", {"start": v(-181.5, -23) * mm, "end": v(-181.39, -22.43) * mm});
            skLineSegment(sketch, "E329", {"start": v(-181.39, -22.43) * mm, "end": v(-181.06, -21.94) * mm});
            skLineSegment(sketch, "E330", {"start": v(-181.06, -21.94) * mm, "end": v(-180.57, -21.61) * mm});
            skLineSegment(sketch, "E331", {"start": v(-180.57, -21.61) * mm, "end": v(-180, -21.5) * mm});
            skLineSegment(sketch, "E332", {"start": v(-180, -21.5) * mm, "end": v(-179.43, -21.61) * mm});
            skLineSegment(sketch, "E333", {"start": v(-179.43, -21.61) * mm, "end": v(-178.94, -21.94) * mm});
            skLineSegment(sketch, "E334", {"start": v(-178.94, -21.94) * mm, "end": v(-178.61, -22.43) * mm});
            skLineSegment(sketch, "E335", {"start": v(-178.61, -22.43) * mm, "end": v(-178.5, -23) * mm});
            skLineSegment(sketch, "E336", {"start": v(-163.5, -165) * mm, "end": v(-163.61, -165.57) * mm});
            skLineSegment(sketch, "E337", {"start": v(-163.61, -165.57) * mm, "end": v(-163.94, -166.06) * mm});
            skLineSegment(sketch, "E338", {"start": v(-163.94, -166.06) * mm, "end": v(-164.43, -166.39) * mm});
            skLineSegment(sketch, "E339", {"start": v(-164.43, -166.39) * mm, "end": v(-165, -166.5) * mm});
            skLineSegment(sketch, "E340", {"start": v(-165, -166.5) * mm, "end": v(-165.57, -166.39) * mm});
            skLineSegment(sketch, "E341", {"start": v(-165.57, -166.39) * mm, "end": v(-166.06, -166.06) * mm});
            skLineSegment(sketch, "E342", {"start": v(-166.06, -166.06) * mm, "end": v(-166.39, -165.57) * mm});
            skLineSegment(sketch, "E343", {"start": v(-166.39, -165.57) * mm, "end": v(-166.5, -165) * mm});
            skLineSegment(sketch, "E344", {"start": v(-166.5, -165) * mm, "end": v(-166.39, -164.43) * mm});
            skLineSegment(sketch, "E345", {"start": v(-166.39, -164.43) * mm, "end": v(-166.06, -163.94) * mm});
            skLineSegment(sketch, "E346", {"start": v(-166.06, -163.94) * mm, "end": v(-165.57, -163.61) * mm});
            skLineSegment(sketch, "E347", {"start": v(-165.57, -163.61) * mm, "end": v(-165, -163.5) * mm});
            skLineSegment(sketch, "E348", {"start": v(-165, -163.5) * mm, "end": v(-164.43, -163.61) * mm});
            skLineSegment(sketch, "E349", {"start": v(-164.43, -163.61) * mm, "end": v(-163.94, -163.94) * mm});
            skLineSegment(sketch, "E350", {"start": v(-163.94, -163.94) * mm, "end": v(-163.61, -164.43) * mm});
            skLineSegment(sketch, "E351", {"start": v(-163.61, -164.43) * mm, "end": v(-163.5, -165) * mm});
            skLineSegment(sketch, "E352", {"start": v(130, -131.5) * mm, "end": v(124.5, -137) * mm});
            skLineSegment(sketch, "E353", {"start": v(124.5, -137) * mm, "end": v(103, -137) * mm});
            skLineSegment(sketch, "E354", {"start": v(103, -137) * mm, "end": v(90, -150) * mm});
            skLineSegment(sketch, "E355", {"start": v(90, -150) * mm, "end": v(90, -165) * mm});
            skLineSegment(sketch, "E356", {"start": v(90, -165) * mm, "end": v(89.62, -166.91) * mm});
            skLineSegment(sketch, "E357", {"start": v(89.62, -166.91) * mm, "end": v(88.54, -168.54) * mm});
            skLineSegment(sketch, "E358", {"start": v(88.54, -168.54) * mm, "end": v(86.91, -169.62) * mm});
            skLineSegment(sketch, "E359", {"start": v(86.91, -169.62) * mm, "end": v(85, -170) * mm});
            skLineSegment(sketch, "E360", {"start": v(85, -170) * mm, "end": v(83.09, -169.62) * mm});
            skLineSegment(sketch, "E361", {"start": v(83.09, -169.62) * mm, "end": v(81.46, -168.54) * mm});
            skLineSegment(sketch, "E362", {"start": v(81.46, -168.54) * mm, "end": v(80.38, -166.91) * mm});
            skLineSegment(sketch, "E363", {"start": v(80.38, -166.91) * mm, "end": v(80, -165) * mm});
            skLineSegment(sketch, "E364", {"start": v(80, -165) * mm, "end": v(80, -150) * mm});
            skLineSegment(sketch, "E365", {"start": v(80, -150) * mm, "end": v(75, -145) * mm});
            skLineSegment(sketch, "E366", {"start": v(75, -145) * mm, "end": v(30, -145) * mm});
            skLineSegment(sketch, "E367", {"start": v(30, -145) * mm, "end": v(5, -170) * mm});
            skLineSegment(sketch, "E368", {"start": v(5, -170) * mm, "end": v(-5, -170) * mm});
            skLineSegment(sketch, "E369", {"start": v(-5, -170) * mm, "end": v(-30, -145) * mm});
            skLineSegment(sketch, "E370", {"start": v(-30, -145) * mm, "end": v(-75, -145) * mm});
            skLineSegment(sketch, "E371", {"start": v(-75, -145) * mm, "end": v(-80, -150) * mm});
            skLineSegment(sketch, "E372", {"start": v(-80, -150) * mm, "end": v(-80, -165) * mm});
            skLineSegment(sketch, "E373", {"start": v(-80, -165) * mm, "end": v(-80.38, -166.91) * mm});
            skLineSegment(sketch, "E374", {"start": v(-80.38, -166.91) * mm, "end": v(-81.46, -168.54) * mm});
            skLineSegment(sketch, "E375", {"start": v(-81.46, -168.54) * mm, "end": v(-83.09, -169.62) * mm});
            skLineSegment(sketch, "E376", {"start": v(-83.09, -169.62) * mm, "end": v(-85, -170) * mm});
            skLineSegment(sketch, "E377", {"start": v(-85, -170) * mm, "end": v(-86.91, -169.62) * mm});
            skLineSegment(sketch, "E378", {"start": v(-86.91, -169.62) * mm, "end": v(-88.54, -168.54) * mm});
            skLineSegment(sketch, "E379", {"start": v(-88.54, -168.54) * mm, "end": v(-89.62, -166.91) * mm});
            skLineSegment(sketch, "E380", {"start": v(-89.62, -166.91) * mm, "end": v(-90, -165) * mm});
            skLineSegment(sketch, "E381", {"start": v(-90, -165) * mm, "end": v(-90, -150) * mm});
            skLineSegment(sketch, "E382", {"start": v(-90, -150) * mm, "end": v(-103, -137) * mm});
            skLineSegment(sketch, "E383", {"start": v(-103, -137) * mm, "end": v(-124.5, -137) * mm});
            skLineSegment(sketch, "E384", {"start": v(-124.5, -137) * mm, "end": v(-129.5, -132) * mm});
            skLineSegment(sketch, "E385", {"start": v(-129.5, -132) * mm, "end": v(-129.5, 139.8) * mm});
            skLineSegment(sketch, "E386", {"start": v(-129.5, 139.8) * mm, "end": v(-124.5, 144.8) * mm});
            skLineSegment(sketch, "E387", {"start": v(-124.5, 144.8) * mm, "end": v(124.5, 144.8) * mm});
            skLineSegment(sketch, "E388", {"start": v(124.5, 144.8) * mm, "end": v(130, 139.3) * mm});
            skLineSegment(sketch, "E389", {"start": v(130, 139.3) * mm, "end": v(130, -131.5) * mm});
            skLineSegment(sketch, "E390", {"start": v(-43, -179) * mm, "end": v(-43.11, -179.57) * mm});
            skLineSegment(sketch, "E391", {"start": v(-43.11, -179.57) * mm, "end": v(-43.44, -180.06) * mm});
            skLineSegment(sketch, "E392", {"start": v(-43.44, -180.06) * mm, "end": v(-43.93, -180.39) * mm});
            skLineSegment(sketch, "E393", {"start": v(-43.93, -180.39) * mm, "end": v(-44.5, -180.5) * mm});
            skLineSegment(sketch, "E394", {"start": v(-44.5, -180.5) * mm, "end": v(-45.07, -180.39) * mm});
            skLineSegment(sketch, "E395", {"start": v(-45.07, -180.39) * mm, "end": v(-45.56, -180.06) * mm});
            skLineSegment(sketch, "E396", {"start": v(-45.56, -180.06) * mm, "end": v(-45.89, -179.57) * mm});
            skLineSegment(sketch, "E397", {"start": v(-45.89, -179.57) * mm, "end": v(-46, -179) * mm});
            skLineSegment(sketch, "E398", {"start": v(-46, -179) * mm, "end": v(-45.89, -178.43) * mm});
            skLineSegment(sketch, "E399", {"start": v(-45.89, -178.43) * mm, "end": v(-45.56, -177.94) * mm});
            skLineSegment(sketch, "E400", {"start": v(-45.56, -177.94) * mm, "end": v(-45.07, -177.61) * mm});
            skLineSegment(sketch, "E401", {"start": v(-45.07, -177.61) * mm, "end": v(-44.5, -177.5) * mm});
            skLineSegment(sketch, "E402", {"start": v(-44.5, -177.5) * mm, "end": v(-43.93, -177.61) * mm});
            skLineSegment(sketch, "E403", {"start": v(-43.93, -177.61) * mm, "end": v(-43.44, -177.94) * mm});
            skLineSegment(sketch, "E404", {"start": v(-43.44, -177.94) * mm, "end": v(-43.11, -178.43) * mm});
            skLineSegment(sketch, "E405", {"start": v(-43.11, -178.43) * mm, "end": v(-43, -179) * mm});
            skLineSegment(sketch, "E406", {"start": v(47, -179) * mm, "end": v(46.89, -179.57) * mm});
            skLineSegment(sketch, "E407", {"start": v(46.89, -179.57) * mm, "end": v(46.56, -180.06) * mm});
            skLineSegment(sketch, "E408", {"start": v(46.56, -180.06) * mm, "end": v(46.07, -180.39) * mm});
            skLineSegment(sketch, "E409", {"start": v(46.07, -180.39) * mm, "end": v(45.5, -180.5) * mm});
            skLineSegment(sketch, "E410", {"start": v(45.5, -180.5) * mm, "end": v(44.93, -180.39) * mm});
            skLineSegment(sketch, "E411", {"start": v(44.93, -180.39) * mm, "end": v(44.44, -180.06) * mm});
            skLineSegment(sketch, "E412", {"start": v(44.44, -180.06) * mm, "end": v(44.11, -179.57) * mm});
            skLineSegment(sketch, "E413", {"start": v(44.11, -179.57) * mm, "end": v(44, -179) * mm});
            skLineSegment(sketch, "E414", {"start": v(44, -179) * mm, "end": v(44.11, -178.43) * mm});
            skLineSegment(sketch, "E415", {"start": v(44.11, -178.43) * mm, "end": v(44.44, -177.94) * mm});
            skLineSegment(sketch, "E416", {"start": v(44.44, -177.94) * mm, "end": v(44.93, -177.61) * mm});
            skLineSegment(sketch, "E417", {"start": v(44.93, -177.61) * mm, "end": v(45.5, -177.5) * mm});
            skLineSegment(sketch, "E418", {"start": v(45.5, -177.5) * mm, "end": v(46.07, -177.61) * mm});
            skLineSegment(sketch, "E419", {"start": v(46.07, -177.61) * mm, "end": v(46.56, -177.94) * mm});
            skLineSegment(sketch, "E420", {"start": v(46.56, -177.94) * mm, "end": v(46.89, -178.43) * mm});
            skLineSegment(sketch, "E421", {"start": v(46.89, -178.43) * mm, "end": v(47, -179) * mm});
            skLineSegment(sketch, "E422", {"start": v(-133, -179) * mm, "end": v(-133.11, -179.57) * mm});
            skLineSegment(sketch, "E423", {"start": v(-133.11, -179.57) * mm, "end": v(-133.44, -180.06) * mm});
            skLineSegment(sketch, "E424", {"start": v(-133.44, -180.06) * mm, "end": v(-133.93, -180.39) * mm});
            skLineSegment(sketch, "E425", {"start": v(-133.93, -180.39) * mm, "end": v(-134.5, -180.5) * mm});
            skLineSegment(sketch, "E426", {"start": v(-134.5, -180.5) * mm, "end": v(-135.07, -180.39) * mm});
            skLineSegment(sketch, "E427", {"start": v(-135.07, -180.39) * mm, "end": v(-135.56, -180.06) * mm});
            skLineSegment(sketch, "E428", {"start": v(-135.56, -180.06) * mm, "end": v(-135.89, -179.57) * mm});
            skLineSegment(sketch, "E429", {"start": v(-135.89, -179.57) * mm, "end": v(-136, -179) * mm});
            skLineSegment(sketch, "E430", {"start": v(-136, -179) * mm, "end": v(-135.89, -178.43) * mm});
            skLineSegment(sketch, "E431", {"start": v(-135.89, -178.43) * mm, "end": v(-135.56, -177.94) * mm});
            skLineSegment(sketch, "E432", {"start": v(-135.56, -177.94) * mm, "end": v(-135.07, -177.61) * mm});
            skLineSegment(sketch, "E433", {"start": v(-135.07, -177.61) * mm, "end": v(-134.5, -177.5) * mm});
            skLineSegment(sketch, "E434", {"start": v(-134.5, -177.5) * mm, "end": v(-133.93, -177.61) * mm});
            skLineSegment(sketch, "E435", {"start": v(-133.93, -177.61) * mm, "end": v(-133.44, -177.94) * mm});
            skLineSegment(sketch, "E436", {"start": v(-133.44, -177.94) * mm, "end": v(-133.11, -178.43) * mm});
            skLineSegment(sketch, "E437", {"start": v(-133.11, -178.43) * mm, "end": v(-133, -179) * mm});
            skLineSegment(sketch, "E438", {"start": v(-135.5, -117) * mm, "end": v(-135.61, -117.57) * mm});
            skLineSegment(sketch, "E439", {"start": v(-135.61, -117.57) * mm, "end": v(-135.94, -118.06) * mm});
            skLineSegment(sketch, "E440", {"start": v(-135.94, -118.06) * mm, "end": v(-136.43, -118.39) * mm});
            skLineSegment(sketch, "E441", {"start": v(-136.43, -118.39) * mm, "end": v(-137, -118.5) * mm});
            skLineSegment(sketch, "E442", {"start": v(-137, -118.5) * mm, "end": v(-137.57, -118.39) * mm});
            skLineSegment(sketch, "E443", {"start": v(-137.57, -118.39) * mm, "end": v(-138.06, -118.06) * mm});
            skLineSegment(sketch, "E444", {"start": v(-138.06, -118.06) * mm, "end": v(-138.39, -117.57) * mm});
            skLineSegment(sketch, "E445", {"start": v(-138.39, -117.57) * mm, "end": v(-138.5, -117) * mm});
            skLineSegment(sketch, "E446", {"start": v(-138.5, -117) * mm, "end": v(-138.39, -116.43) * mm});
            skLineSegment(sketch, "E447", {"start": v(-138.39, -116.43) * mm, "end": v(-138.06, -115.94) * mm});
            skLineSegment(sketch, "E448", {"start": v(-138.06, -115.94) * mm, "end": v(-137.57, -115.61) * mm});
            skLineSegment(sketch, "E449", {"start": v(-137.57, -115.61) * mm, "end": v(-137, -115.5) * mm});
            skLineSegment(sketch, "E450", {"start": v(-137, -115.5) * mm, "end": v(-136.43, -115.61) * mm});
            skLineSegment(sketch, "E451", {"start": v(-136.43, -115.61) * mm, "end": v(-135.94, -115.94) * mm});
            skLineSegment(sketch, "E452", {"start": v(-135.94, -115.94) * mm, "end": v(-135.61, -116.43) * mm});
            skLineSegment(sketch, "E453", {"start": v(-135.61, -116.43) * mm, "end": v(-135.5, -117) * mm});
            skLineSegment(sketch, "E454", {"start": v(180, 185) * mm, "end": v(-180, 185) * mm});
            skLineSegment(sketch, "E455", {"start": v(-185, 180) * mm, "end": v(-180, 185) * mm});
            skLineSegment(sketch, "E456", {"start": v(-185, -180) * mm, "end": v(-185, 180) * mm});
            skLineSegment(sketch, "E457", {"start": v(-185, -180) * mm, "end": v(-180, -185) * mm});
            skLineSegment(sketch, "E458", {"start": v(-180, -185) * mm, "end": v(-160, -185) * mm});
            skLineSegment(sketch, "E459", {"start": v(-160, -185) * mm, "end": v(-155.17, -180.17) * mm});
            skLineSegment(sketch, "E460", {"start": v(-155.17, -180.17) * mm, "end": v(-153.87, -179.3) * mm});
            skLineSegment(sketch, "E461", {"start": v(-153.87, -179.3) * mm, "end": v(-152.34, -179) * mm});
            skLineSegment(sketch, "E462", {"start": v(-152.34, -179) * mm, "end": v(-150.16, -179) * mm});
            skLineSegment(sketch, "E463", {"start": v(-150.16, -179) * mm, "end": v(-148.63, -179.3) * mm});
            skLineSegment(sketch, "E464", {"start": v(-148.63, -179.3) * mm, "end": v(-147.33, -180.17) * mm});
            skLineSegment(sketch, "E465", {"start": v(-147.33, -180.17) * mm, "end": v(-144.5, -183) * mm});
            skLineSegment(sketch, "E466", {"start": v(-144.5, -183) * mm, "end": v(144.5, -183) * mm});
            skLineSegment(sketch, "E467", {"start": v(144.5, -183) * mm, "end": v(147.33, -180.17) * mm});
            skLineSegment(sketch, "E468", {"start": v(147.33, -180.17) * mm, "end": v(148.63, -179.3) * mm});
            skLineSegment(sketch, "E469", {"start": v(148.63, -179.3) * mm, "end": v(150.16, -179) * mm});
            skLineSegment(sketch, "E470", {"start": v(150.16, -179) * mm, "end": v(152.34, -179) * mm});
            skLineSegment(sketch, "E471", {"start": v(152.34, -179) * mm, "end": v(153.87, -179.3) * mm});
            skLineSegment(sketch, "E472", {"start": v(153.87, -179.3) * mm, "end": v(155.17, -180.17) * mm});
            skLineSegment(sketch, "E473", {"start": v(155.17, -180.17) * mm, "end": v(160, -185) * mm});
            skLineSegment(sketch, "E474", {"start": v(160, -185) * mm, "end": v(180, -185) * mm});
            skLineSegment(sketch, "E475", {"start": v(180, -185) * mm, "end": v(185, -180) * mm});
            skLineSegment(sketch, "E476", {"start": v(185, -180) * mm, "end": v(185, 180) * mm});
            skLineSegment(sketch, "E477", {"start": v(185, 180) * mm, "end": v(180, 185) * mm});
            skSolve(sketch);
        }
        {
            var Q0;
            Q0=makeQuery(id+"F0.imprint","IMPRINT",FACE,{"disambiguationData":[TD([[makeQuery(id+"F0.imprint","IMPRINT",EDGE,{"derivedFrom":sQuery(id+"F0.wireOp",EDGE,"E0")}),1.0]])]});
            extrude(context, id + "F1", {"entities" : qUnion([Q0]), "depth" : 6 * mm, "offsetDistance" : 25 * mm});
        }
    });
